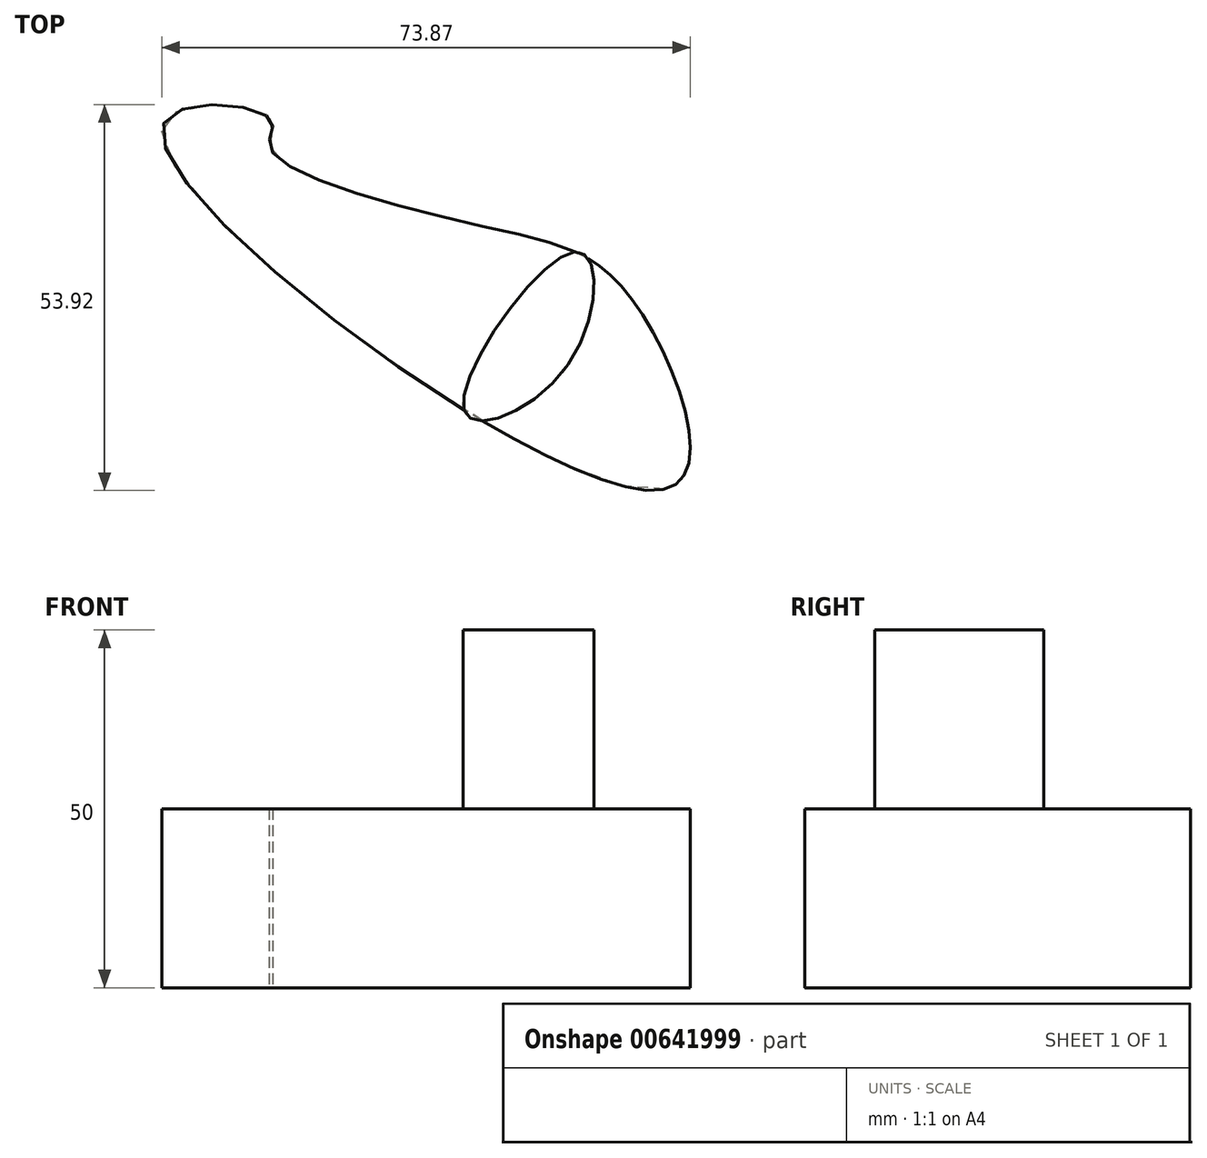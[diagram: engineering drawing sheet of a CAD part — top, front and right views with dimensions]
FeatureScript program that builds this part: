
annotation { "Feature Type Name" : "Feature", "Feature Type Description" : "" }
export const myFeature = defineFeature(function(context is Context, id is Id, definition is map)
    precondition{}
    {
        {
            var Q0;
            Q0=qCreatedBy(makeId("Top.planeOp"),FACE);
            var sketch = newSketch(context, id + "F0", { "sketchPlane" : qUnion([Q0])});
            skFitSpline(sketch, "E0", {"points": [v(55.16, 0) * mm, v(49.87, -27.76) * mm, v(22.47, -37.14) * mm, v(-31.85, -12.62) * mm, v(-23.43, 42.44) * mm], "startDerivative": vector(-3.92, -153.04) * mm, "endDerivative": vector(87.5, 211.27) * mm});
            skFitSpline(sketch, "E1", {"points": [v(0, 47.73) * mm, v(31.12, 36.43) * mm, v(51.07, 25.85) * mm, v(55.16, 0) * mm, v(-15.02, 50.62) * mm, v(0, 51.82) * mm, v(0, 47.73) * mm]});
            skSolve(sketch);
        }
        {
            var Q0;
            Q0 = qSketchRegion(id + "F0", true);
            extrude(context, id + "F1", {"entities" : qUnion([Q0]), "depth" : 25 * mm, "offsetDistance" : 25 * mm});
        }
        {
            var Q0;
            Q0=makeQuery(id+"F1.opExtrude","CAP_FACE",FACE,{"disambiguationData":[OSD([sQuery(id+"F0.wireOp",EDGE,"E1")])],"isStart":false});
            var sketch = newSketch(context, id + "F2", { "sketchPlane" : qUnion([Q0])});
            skFitSpline(sketch, "E2", {"points": [v(27.12, 11.1) * mm, v(42.68, 33.18) * mm, v(41.46, 17.12) * mm, v(27.12, 11.1) * mm]});
            skSolve(sketch);
        }
        {
            var Q0;
            Q0 = qSketchRegion(id + "F2", true);
            extrude(context, id + "F3", {"entities" : qUnion([Q0]), "operationType" : NewBodyOperationType.ADD, "depth" : 25 * mm, "offsetDistance" : 25 * mm});
        }
    });
